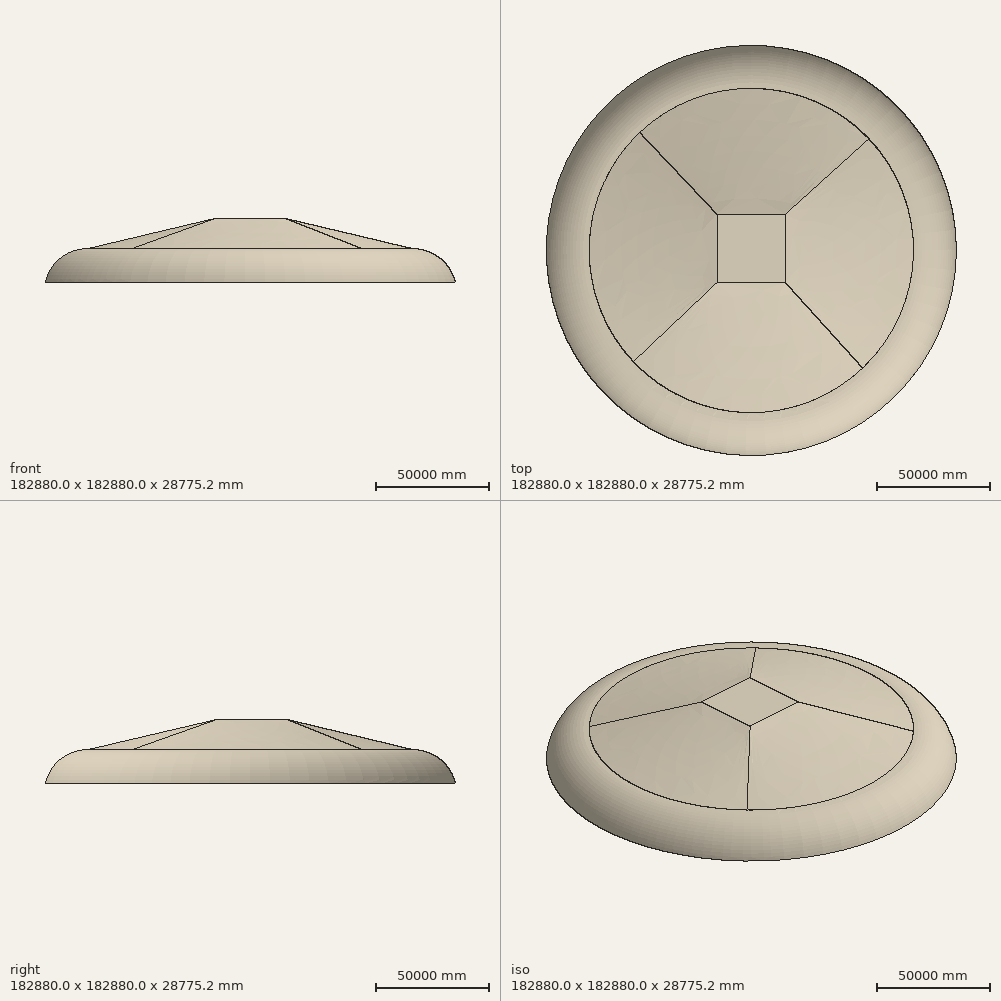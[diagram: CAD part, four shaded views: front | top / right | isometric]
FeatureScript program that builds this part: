
annotation { "Feature Type Name" : "Feature", "Feature Type Description" : "" }
export const myFeature = defineFeature(function(context is Context, id is Id, definition is map)
    precondition{}
    {
        {
            var Q0;
            Q0=qCreatedBy(makeId("Right.planeOp"),FACE);
            var sketch = newSketch(context, id + "F0", { "sketchPlane" : qUnion([Q0])});
            skLineSegment(sketch, "E0.bottom", {"start": v(-91440, -7620) * mm, "end": v(91440, -7620) * mm});
            skLineSegment(sketch, "E0.top", {"start": v(-91440, 7620) * mm, "end": v(91440, 7620) * mm});
            skLineSegment(sketch, "E0.left", {"start": v(-91440, -7620) * mm, "end": v(-91440, 7620) * mm});
            skLineSegment(sketch, "E0.right", {"start": v(91440, -7620) * mm, "end": v(91440, 7620) * mm});
            skPoint(sketch, "E0.middle", {"position": v(0, 0) * mm});
            skLineSegment(sketch, "E1", {"start": v(0, 0) * mm, "end": v(0, -7620) * mm});
            skLineSegment(sketch, "E2", {"start": v(0, -7620) * mm, "end": v(0, 7620) * mm});
            skSolve(sketch);
        }
        {
            var Q0;
            {var subQ4=sQuery(id+"F0.wireOp",EDGE,"E0.left");Q0=makeQuery(id+"F0.imprint","IMPRINT",FACE,{"disambiguationData":[TD([[makeQuery(id+"F0.imprint","IMPRINT",EDGE,{"derivedFrom":subQ4}),-1.0]])]});}
            var Q1;
            Q1=sQuery(id+"F0.wireOp",EDGE,"E2");
            revolve(context, id + "F1", {"entities" : qUnion([Q0]), "axis" : qUnion([Q1]), "revolveType" : RevolveType.FULL, "oppositeDirection" : true});
        }
        {
            var Q0;
            Q0=makeQuery(id+"F1.opRevolve","SWEPT_EDGE",EDGE,{"disambiguationData":[OSD([sQuery(id+"F0.wireOp",EDGE,"E0.top"),sQuery(id+"F0.wireOp",EDGE,"E0.left")])]});
            fillet(context, id + "F2", {"entities" : qUnion([Q0]), "radius" : 19622.73 * mm, "tangentPropagation" : true, "allowEdgeOverflow" : false});
        }
        {
            var Q0;
            Q0=qCreatedBy(makeId("Right.planeOp"),FACE);
            var sketch = newSketch(context, id + "F3", { "sketchPlane" : qUnion([Q0])});
            skLineSegment(sketch, "E3", {"start": v(-14426.34, 21155.19) * mm, "end": v(16053.66, 21155.19) * mm});
            skSolve(sketch);
        }
        {
            var Q0;
            Q0=sQuery(id+"F3.wireOp",EDGE,"E3");
            extrude(context, id + "F4", {"bodyType" : ToolBodyType.SURFACE, "surfaceEntities" : qUnion([Q0]), "endBound" : BoundingType.SYMMETRIC, "depth" : 30480 * mm, "offsetDistance" : 25.4 * mm});
        }
        {
            var Q0;
            Q0=makeQuery(id+"F1.opRevolve","SWEPT_FACE",FACE,{"disambiguationData":[OSD([sQuery(id+"F0.wireOp",EDGE,"E0.top")])]});
            var Q1;
            Q1=makeQuery(id+"F4.opExtrude","SWEPT_FACE",FACE,{"disambiguationData":[OSD([sQuery(id+"F3.wireOp",EDGE,"E3")])]});
            loft(context, id + "F5", {"sheetProfilesArray" : [{ "sheetProfileEntities" : qUnion([Q0]) }, { "sheetProfileEntities" : qUnion([Q1]) }]});
        }
    });
